# Revit family: 306_a738968fd52444bc80b2e293ebf0c3
name_source: partatom
category: Pipe Accessories
units: mm (PartAtom-declared; Revit-internal decimal feet)

## family parameters
Always vertical = Yes
Cut with Voids When Loaded = No
Part Type = Valve - Breaks Into
Round Connector Dimension = Use Diameter
Shared = No
Work Plane-Based = No

## types (4) — shared parameters
AL1 = 100 mm
AL2 = 58 mm
AL3 = 128 mm
AL3__ve = -128 mm  [stored -0.419948 ft]
ALR = 16 mm  [stored 0.0524934 ft]
ALR__ve = -16 mm  [stored -0.0524934 ft]
CC = 71 mm
CC1 = 45 mm
CC1__ve = -45 mm  [stored -0.147638 ft]
CenSd_RNR_6 = 7 mm  [stored 0.0229659 ft]
Description = Chr.-pl. divert. 3-way zone valve, 230V actuator, M-M conn.
G1 = 31 mm  [stored 0.101706 ft]
G2 = 44 mm
GG = 58 mm
GG__ve = -58 mm  [stored -0.190289 ft]
KLR = 12 mm  [stored 0.0393701 ft]
KT = 22 mm  [stored 0.0721785 ft]
KT1 = 18 mm
KT11 = 16 mm  [stored 0.0524934 ft]
L2D = 163 mm
L2D_Min = 3048 mm
Manufacturer = FAR
NR2 = 35 mm  [stored 0.114829 ft]
QmdConnectorList = 301;D;302;D
RH = 4 mm  [stored 0.0131234 ft]
RNR = 8 mm  [stored 0.0262467 ft]
RT2 = 32 mm
RW = 6 mm  [stored 0.019685 ft]
SW2 = No
TRH = 6 mm  [stored 0.019685 ft]
TS = 20 mm  [stored 0.0656168 ft]
TS__ve = -20 mm  [stored -0.0656168 ft]
W2D = 40 mm
magiPartTypeId = 306
magiProductFamilyId = a738968fd52444bc80b2e293ebf0c3

## per-type parameters (varying)
- 303920 112 30: B0=37 mm; B1=5 mm  [stored 0.0164042 ft]; B2=11 mm; B22=9 mm  [stored 0.0295276 ft]; BR=19 mm  [stored 0.062336 ft]; BR1=15 mm  [stored 0.0492126 ft]; CenSd_NR1_6=26 mm; CenSd_NRS1_6=9 mm  [stored 0.0295276 ft]; CenSd_NR_6=30 mm  [stored 0.0984252 ft]; D=40 mm; HB=78 mm; HB1=42 mm; HB1__ve=-42 mm; I=96 mm; L1=8 mm  [stored 0.0262467 ft]; L1__ve=-8 mm; L2=82 mm; LR=33 mm; LR__ve=-33 mm; NR=35 mm  [stored 0.114829 ft]; NR1=30 mm  [stored 0.0984252 ft]; NRS1=10 mm  [stored 0.0328084 ft]; NT=16 mm  [stored 0.0524934 ft]; NT__ve=-16 mm  [stored -0.0524934 ft]; R=20 mm  [stored 0.0656168 ft]; RT=24 mm  [stored 0.0787402 ft]; RT1=29 mm  [stored 0.0951444 ft]; RT11=22 mm  [stored 0.0721785 ft]; magiProductId=aa87dcb57c834a73871330672e90bd
- 303920 112 80: B0=37 mm; B1=5 mm  [stored 0.0164042 ft]; B2=11 mm; B22=9 mm  [stored 0.0295276 ft]; BR=19 mm  [stored 0.062336 ft]; BR1=15 mm  [stored 0.0492126 ft]; CenSd_NR1_6=26 mm; CenSd_NRS1_6=9 mm  [stored 0.0295276 ft]; CenSd_NR_6=30 mm  [stored 0.0984252 ft]; D=40 mm; HB=78 mm; HB1=42 mm; HB1__ve=-42 mm; I=96 mm; L1=8 mm  [stored 0.0262467 ft]; L1__ve=-8 mm; L2=82 mm; LR=33 mm; LR__ve=-33 mm; NR=35 mm  [stored 0.114829 ft]; NR1=30 mm  [stored 0.0984252 ft]; NRS1=10 mm  [stored 0.0328084 ft]; NT=16 mm  [stored 0.0524934 ft]; NT__ve=-16 mm  [stored -0.0524934 ft]; R=20 mm  [stored 0.0656168 ft]; RT=24 mm  [stored 0.0787402 ft]; RT1=29 mm  [stored 0.0951444 ft]; RT11=22 mm  [stored 0.0721785 ft]; magiProductId=68b1e0ba9f7f44a1af7a8b1974f58f
- 303920 2 30: B0=38 mm; B1=6 mm  [stored 0.019685 ft]; B2=17 mm; B22=15 mm  [stored 0.0492126 ft]; BR=24 mm  [stored 0.0787402 ft]; BR1=19 mm  [stored 0.062336 ft]; CenSd_NR1_6=32 mm; CenSd_NRS1_6=11 mm; CenSd_NR_6=38 mm; D=50 mm; HB=90 mm; HB1=51 mm; HB1__ve=-51 mm; I=113 mm; L1=10 mm  [stored 0.0328084 ft]; L1__ve=-10 mm  [stored -0.0328084 ft]; L2=96 mm; LR=46 mm; LR__ve=-46 mm; NR=44 mm; NR1=38 mm; NRS1=13 mm  [stored 0.0426509 ft]; NT=19 mm  [stored 0.062336 ft]; NT__ve=-19 mm  [stored -0.062336 ft]; R=25 mm  [stored 0.082021 ft]; RT=30 mm  [stored 0.0984252 ft]; RT1=36 mm; RT11=27 mm; magiProductId=3d514ac281df41cc8924a5acd76e82
- 303920 2 80: B0=38 mm; B1=6 mm  [stored 0.019685 ft]; B2=17 mm; B22=15 mm  [stored 0.0492126 ft]; BR=24 mm  [stored 0.0787402 ft]; BR1=19 mm  [stored 0.062336 ft]; CenSd_NR1_6=32 mm; CenSd_NRS1_6=11 mm; CenSd_NR_6=38 mm; D=50 mm; HB=90 mm; HB1=51 mm; HB1__ve=-51 mm; I=113 mm; L1=10 mm  [stored 0.0328084 ft]; L1__ve=-10 mm  [stored -0.0328084 ft]; L2=96 mm; LR=46 mm; LR__ve=-46 mm; NR=44 mm; NR1=38 mm; NRS1=13 mm  [stored 0.0426509 ft]; NT=19 mm  [stored 0.062336 ft]; NT__ve=-19 mm  [stored -0.062336 ft]; R=25 mm  [stored 0.082021 ft]; RT=30 mm  [stored 0.0984252 ft]; RT1=36 mm; RT11=27 mm; magiProductId=872329ede6f54276bd5c2a1d78cc35

note: column(s) folded — value = type name in every type: MC Product Code

note: [stored X ft] marks values corroborated as IEEE doubles in the binary element streams (Revit-internal decimal feet)

## geometry (parser evidence)
native form markers: Sweep x3
no freeform markers — native parametric forms only
